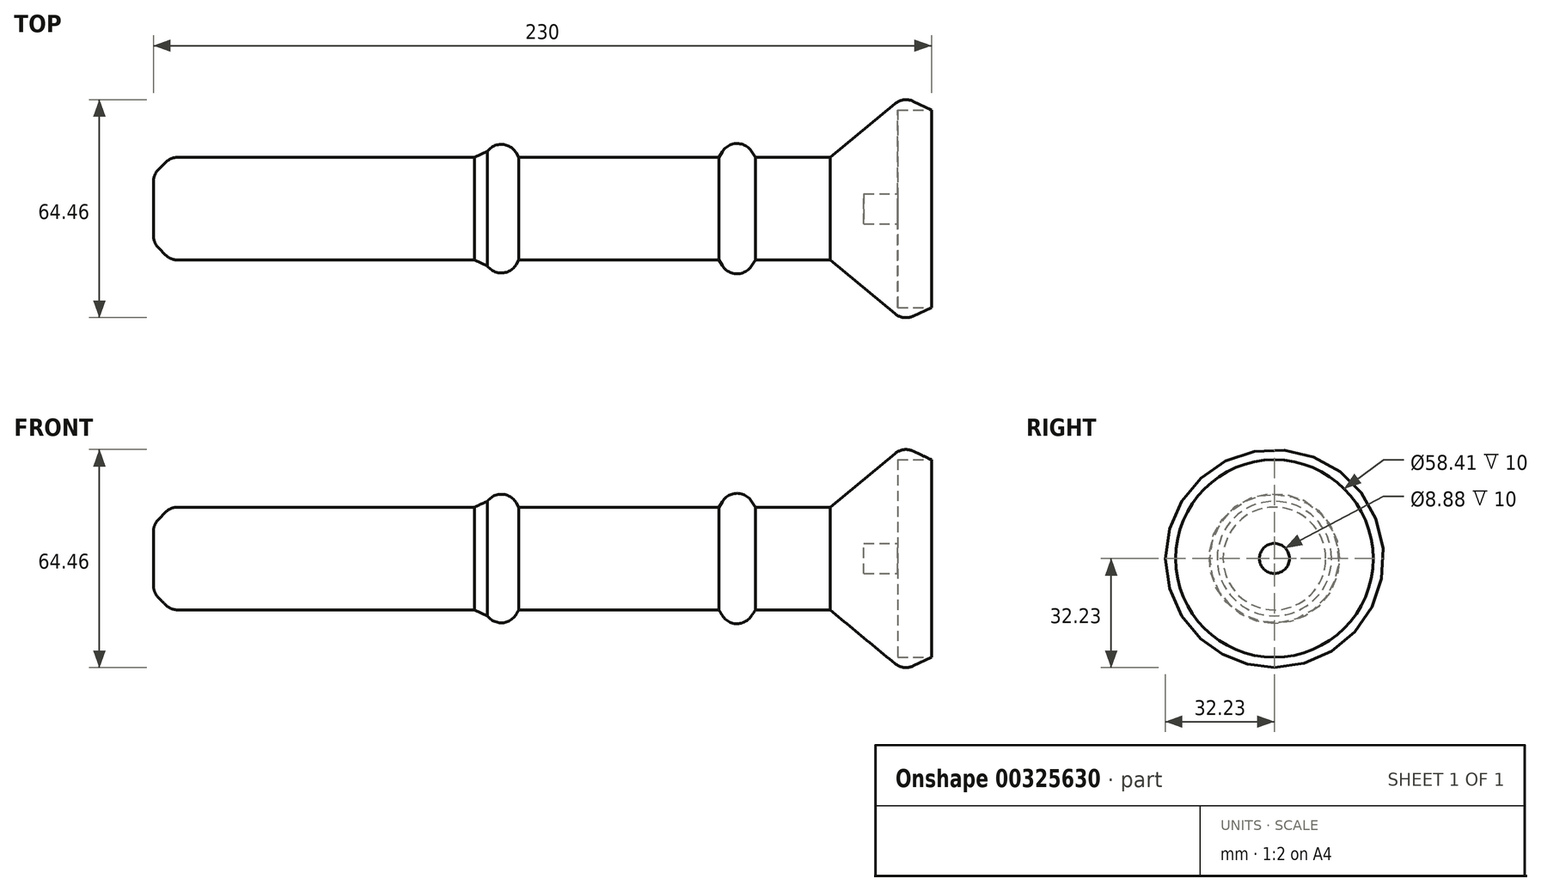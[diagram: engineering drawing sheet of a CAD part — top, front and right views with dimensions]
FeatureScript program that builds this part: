
annotation { "Feature Type Name" : "Feature", "Feature Type Description" : "" }
export const myFeature = defineFeature(function(context is Context, id is Id, definition is map)
    precondition{}
    {
        {
            var Q0;
            Q0=qCreatedBy(makeId("Front.planeOp"),FACE);
            var sketch = newSketch(context, id + "F0", { "sketchPlane" : qUnion([Q0])});
            skLineSegment(sketch, "E0", {"start": v(0, 0) * mm, "end": v(0, 15.2) * mm});
            skLineSegment(sketch, "E1", {"start": v(200, 15.2) * mm, "end": v(230, 40) * mm});
            skLineSegment(sketch, "E2", {"start": v(230, 40) * mm, "end": v(230, 0) * mm});
            skLineSegment(sketch, "E3", {"start": v(230, 0) * mm, "end": v(0, 0) * mm});
            skLineSegment(sketch, "E4", {"start": v(0, 15.2) * mm, "end": v(97.18, 15.2) * mm});
            skLineSegment(sketch, "E5", {"start": v(177.97, 15.2) * mm, "end": v(172.22, 23.55) * mm});
            skLineSegment(sketch, "E6", {"start": v(172.22, 23.55) * mm, "end": v(167.15, 15.2) * mm});
            skLineSegment(sketch, "E7", {"start": v(108, 15.2) * mm, "end": v(103.6, 22.53) * mm});
            skLineSegment(sketch, "E8", {"start": v(103.6, 22.53) * mm, "end": v(97.18, 15.2) * mm});
            skLineSegment(sketch, "E9.trimOffspring", {"start": v(108, 15.2) * mm, "end": v(167.15, 15.2) * mm});
            skLineSegment(sketch, "E10.trimOffspring", {"start": v(177.97, 15.2) * mm, "end": v(200, 15.2) * mm});
            skSolve(sketch);
        }
        {
            var Q0;
            Q0=makeQuery(id+"F0.imprint","IMPRINT",FACE,{"disambiguationData":[TD([[makeQuery(id+"F0.imprint","IMPRINT",EDGE,{"derivedFrom":sQuery(id+"F0.wireOp",EDGE,"E0")}),-1.0]])]});
            var Q1;
            Q1=sQuery(id+"F0.wireOp",EDGE,"E3");
            revolve(context, id + "F1", {"entities" : qUnion([Q0]), "axis" : qUnion([Q1]), "revolveType" : RevolveType.FULL});
        }
        {
            var Q0;
            Q0=makeQuery(id+"F1.opRevolve","SWEPT_EDGE",EDGE,{"disambiguationData":[OSD([sQuery(id+"F0.wireOp",EDGE,"E7"),sQuery(id+"F0.wireOp",EDGE,"E8")])]});
            fillet(context, id + "F2", {"entities" : qUnion([Q0]), "radius" : 5.08 * mm, "tangentPropagation" : true, "allowEdgeOverflow" : false});
        }
        {
            var Q0;
            Q0=makeQuery(id+"F1.opRevolve","SWEPT_EDGE",EDGE,{"disambiguationData":[OSD([sQuery(id+"F0.wireOp",EDGE,"E5"),sQuery(id+"F0.wireOp",EDGE,"E6")])]});
            fillet(context, id + "F3", {"entities" : qUnion([Q0]), "radius" : 5.08 * mm, "tangentPropagation" : true, "allowEdgeOverflow" : false});
        }
        {
            var Q0;
            Q0=makeQuery(id+"F1.opRevolve","SWEPT_FACE",FACE,{"disambiguationData":[OSD([sQuery(id+"F0.wireOp",EDGE,"E4")])]});
            var Q1;
            Q1=makeQuery(id+"F1.opRevolve","SWEPT_EDGE",EDGE,{"disambiguationData":[OSD([sQuery(id+"F0.wireOp",EDGE,"E1"),sQuery(id+"F0.wireOp",EDGE,"E2")])]});
            chamfer(context, id + "F4", {"entities" : qUnion([Q0, Q1]), "width" : 5.08 * mm, "tangentPropagation" : true});
        }
        {
            var Q0;
            {var subQ0=sQuery(id+"F0.wireOp",EDGE,"E1");Q0=makeQuery(id+"F4.opChamfer","BLEND_EDGE",EDGE,{"blendedFrom":[makeQuery(id+"F1.opRevolve","SWEPT_EDGE",EDGE,{"disambiguationData":[OSD([subQ0,sQuery(id+"F0.wireOp",EDGE,"E2")])]}),makeQuery(id+"F1.opRevolve","SWEPT_FACE",FACE,{"disambiguationData":[OSD([subQ0])]})],"blendedInto":[makeQuery(id+"F1.opRevolve","SWEPT_FACE",FACE,{"disambiguationData":[OSD([subQ0])]})]});}
            fillet(context, id + "F5", {"entities" : qUnion([Q0]), "radius" : 5.08 * mm, "tangentPropagation" : true, "allowEdgeOverflow" : false});
        }
        {
            var Q0;
            Q0=makeQuery(id+"F4.opChamfer","BLEND_FACE",FACE,{"disambiguationData":[OSD([sQuery(id+"F0.wireOp",EDGE,"E0"),sQuery(id+"F0.wireOp",EDGE,"E4")])]});
            fillet(context, id + "F6", {"entities" : qUnion([Q0]), "radius" : 5.08 * mm, "tangentPropagation" : true, "allowEdgeOverflow" : false});
        }
        {
            var Q0;
            Q0=makeQuery(id+"F1.opRevolve","SWEPT_FACE",FACE,{"disambiguationData":[OSD([sQuery(id+"F0.wireOp",EDGE,"E2")])]});
            extrude(context, id + "F7", {"entities" : qUnion([Q0]), "operationType" : NewBodyOperationType.REMOVE, "oppositeDirection" : true, "depth" : 10 * mm});
        }
        {
            var Q0;
            Q0=makeQuery(id+"F7.boolean.opBoolean","COPY",FACE,{"derivedFrom":makeQuery(id+"F7.opExtrude","CAP_FACE",FACE,{"disambiguationData":[OSD([sQuery(id+"F0.wireOp",EDGE,"E2")])],"isStart":false})});
            var sketch = newSketch(context, id + "F8", { "sketchPlane" : qUnion([Q0])});
            skCircle(sketch, "E11", {"center": v(0, 0) * mm, "radius": 4.44 * mm});
            skSolve(sketch);
        }
        {
            var Q0;
            Q0=makeQuery(id+"F8.imprint","IMPRINT",FACE,{"disambiguationData":[TD([[makeQuery(id+"F8.imprint","IMPRINT",EDGE,{"derivedFrom":sQuery(id+"F8.wireOp",EDGE,"E11")}),1.0]])]});
            extrude(context, id + "F9", {"entities" : qUnion([Q0]), "operationType" : NewBodyOperationType.REMOVE, "oppositeDirection" : true, "depth" : 10 * mm});
        }
    });
